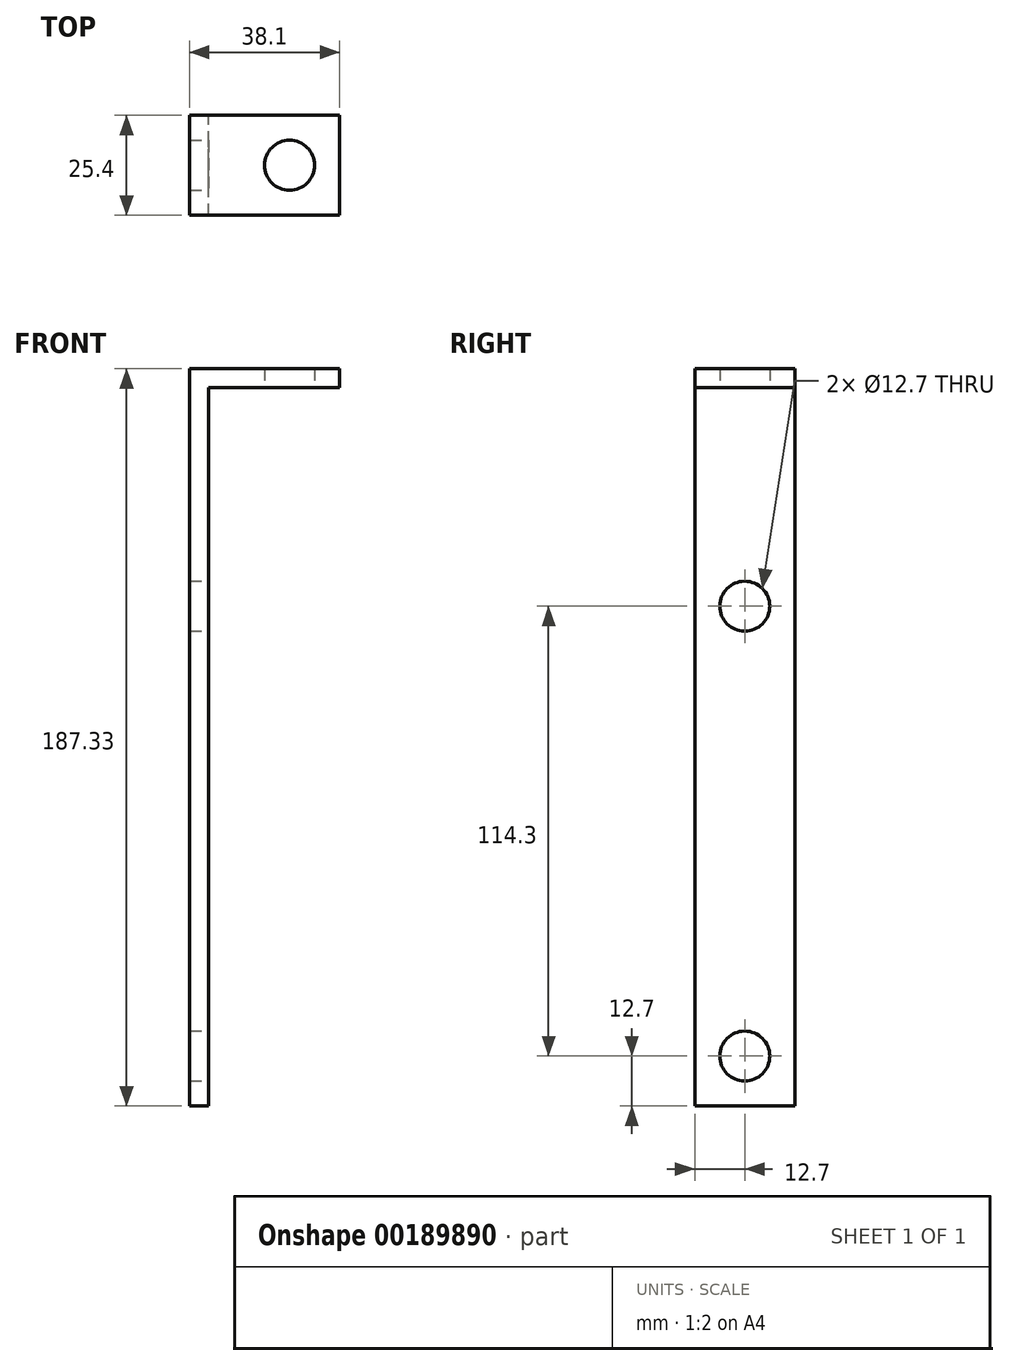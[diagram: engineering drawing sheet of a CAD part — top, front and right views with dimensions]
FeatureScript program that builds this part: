
annotation { "Feature Type Name" : "Feature", "Feature Type Description" : "" }
export const myFeature = defineFeature(function(context is Context, id is Id, definition is map)
    precondition{}
    {
        {
            var Q0;
            Q0=qCreatedBy(makeId("Front.planeOp"),FACE);
            var sketch = newSketch(context, id + "F0", { "sketchPlane" : qUnion([Q0])});
            skLineSegment(sketch, "E0", {"start": v(0, 0) * mm, "end": v(0, 187.33) * mm});
            skLineSegment(sketch, "E1", {"start": v(0, 187.33) * mm, "end": v(38.1, 187.33) * mm});
            skLineSegment(sketch, "E2", {"start": v(38.1, 187.33) * mm, "end": v(38.1, 182.56) * mm});
            skLineSegment(sketch, "E3", {"start": v(38.1, 182.56) * mm, "end": v(4.76, 182.56) * mm});
            skLineSegment(sketch, "E4", {"start": v(4.76, 182.56) * mm, "end": v(4.76, 0) * mm});
            skLineSegment(sketch, "E5", {"start": v(4.76, 0) * mm, "end": v(0, 0) * mm});
            skSolve(sketch);
        }
        {
            var Q0;
            Q0=makeQuery(id+"F0.imprint","IMPRINT",FACE,{"disambiguationData":[TD([[makeQuery(id+"F0.imprint","IMPRINT",EDGE,{"derivedFrom":sQuery(id+"F0.wireOp",EDGE,"E0")}),-1.0]])]});
            extrude(context, id + "F1", {"entities" : qUnion([Q0]), "depth" : 25.4 * mm});
        }
        {
            var Q0;
            Q0=makeQuery(id+"F1.opExtrude","SWEPT_FACE",FACE,{"disambiguationData":[OSD([sQuery(id+"F0.wireOp",EDGE,"E4")])]});
            var sketch = newSketch(context, id + "F2", { "sketchPlane" : qUnion([Q0])});
            skLineSegment(sketch, "E6.0.0", {"start": v(0, 187.33) * mm, "end": v(0, 0) * mm, "construction": true});
            skLineSegment(sketch, "E6.0.1", {"start": v(0, 0) * mm, "end": v(-25.4, 0) * mm, "construction": true});
            skLineSegment(sketch, "E6.0.2", {"start": v(-25.4, 0) * mm, "end": v(-25.4, 187.33) * mm, "construction": true});
            skLineSegment(sketch, "E6.0.3", {"start": v(-25.4, 187.33) * mm, "end": v(0, 187.33) * mm, "construction": true});
            skLineSegment(sketch, "E7", {"start": v(-12.7, 187.33) * mm, "end": v(-12.7, 0) * mm, "construction": true});
            skPoint(sketch, "E8", {"position": v(-12.7, 127) * mm});
            skPoint(sketch, "E9", {"position": v(-12.7, 12.7) * mm});
            skSolve(sketch);
        }
        {
            var Q0;
            Q0=sQuery(id+"F2.wireOp",VERTEX,"E8");
            var Q1;
            Q1=sQuery(id+"F2.wireOp",VERTEX,"E9");
            var Q2;
            Q2=makeQuery(id+"F1.opExtrude","SWEPT_BODY",BODY,{"disambiguationData":[OSD([sQuery(id+"F0.wireOp",EDGE,"E0"),sQuery(id+"F0.wireOp",EDGE,"E1"),sQuery(id+"F0.wireOp",EDGE,"E2"),sQuery(id+"F0.wireOp",EDGE,"E3"),sQuery(id+"F0.wireOp",EDGE,"E4"),sQuery(id+"F0.wireOp",EDGE,"E5")])]});
            hole(context, id + "F3", {"style" : HoleStyle.SIMPLE, "endStyle" : HoleEndStyle.THROUGH, "holeDiameter" : 12.7 * mm, "locations" : qUnion([Q0, Q1]), "scope" : qUnion([Q2]), "isTappedThrough" : true});
        }
        {
            var Q0;
            Q0=makeQuery(id+"F1.opExtrude","SWEPT_FACE",FACE,{"disambiguationData":[OSD([sQuery(id+"F0.wireOp",EDGE,"E3")])]});
            var sketch = newSketch(context, id + "F4", { "sketchPlane" : qUnion([Q0])});
            skLineSegment(sketch, "E10.0.0", {"start": v(38.1, 0) * mm, "end": v(0, 0) * mm, "construction": true});
            skLineSegment(sketch, "E10.0.1", {"start": v(0, 0) * mm, "end": v(0, 25.4) * mm, "construction": true});
            skLineSegment(sketch, "E10.0.2", {"start": v(0, 25.4) * mm, "end": v(38.1, 25.4) * mm, "construction": true});
            skLineSegment(sketch, "E10.0.3", {"start": v(38.1, 25.4) * mm, "end": v(38.1, 0) * mm, "construction": true});
            skLineSegment(sketch, "E11", {"start": v(0, 12.7) * mm, "end": v(38.1, 12.7) * mm, "construction": true});
            skPoint(sketch, "E12", {"position": v(25.4, 12.7) * mm});
            skSolve(sketch);
        }
        {
            var Q0;
            Q0=sQuery(id+"F4.wireOp",VERTEX,"E12");
            var Q1;
            Q1=makeQuery(id+"F1.opExtrude","SWEPT_BODY",BODY,{"disambiguationData":[OSD([sQuery(id+"F0.wireOp",EDGE,"E0"),sQuery(id+"F0.wireOp",EDGE,"E1"),sQuery(id+"F0.wireOp",EDGE,"E2"),sQuery(id+"F0.wireOp",EDGE,"E3"),sQuery(id+"F0.wireOp",EDGE,"E4"),sQuery(id+"F0.wireOp",EDGE,"E5")])]});
            hole(context, id + "F5", {"style" : HoleStyle.SIMPLE, "endStyle" : HoleEndStyle.THROUGH, "holeDiameter" : 12.7 * mm, "locations" : qUnion([Q0]), "scope" : qUnion([Q1]), "isTappedThrough" : true});
        }
    });
